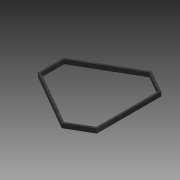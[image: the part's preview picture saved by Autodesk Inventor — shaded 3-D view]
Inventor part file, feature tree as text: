
AUTODESK INVENTOR PART (.ipt)
format: ipt  version: 2015 SP1 (Build 190203100, 203)  size: 87,552 bytes
history: native  units: in
note: dims shown in document units (in); Inventor stores cm internally (conversion verified against a paired STEP export)
features: extrude x1, sketch x1
ambient origin geometry x8: Origin, YZ Plane, XZ Plane, XY Plane, X Axis, Y Axis, Z Axis, Center Point
bodies: Body1 (feature_tree)
feature tree (2):
  extrude  "Extrusion6"  Depth=0.8891in
  sketch  "Sketch1"  dims[d45=2.0in d46=0.0in d47=0.8891in]
